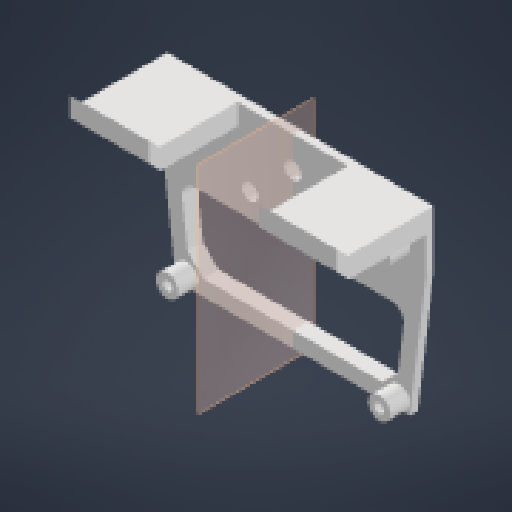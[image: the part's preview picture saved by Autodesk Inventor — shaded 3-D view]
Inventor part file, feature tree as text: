
AUTODESK INVENTOR PART (.ipt)
format: ipt  version: 2024 (Build 280153000, 153)  size: 214,528 bytes
history: native  units: in
note: dims shown in document units (in); Inventor stores cm internally (conversion verified against a paired STEP export)
features: other x4, extrude x3, sketch x3, reference x3, chamfer x2, fillet x1, mirror x1
ambient origin geometry x8: Origin, YZ Plane, XZ Plane, XY Plane, X Axis, Y Axis, Z Axis, Center Point
bodies: Solid1 (feature_tree)
feature tree (17):
  extrude  "Extrusion1"  Depth=0.1575in TaperAngle=0.0deg
  extrude  "Extrusion2"  Depth=1.5748in
  extrude  "Extrusion3"  Depth=0.125in
  chamfer  "Chamfer1"  Distance=1.5748in
  chamfer  "Chamfer2"  Distance=0.0787in
  fillet  "Fillet1"  Radius=0.1122in
  mirror  "Mirror1"
  sketch  "Sketch1"  dims[d0=0.1575in d1=0.1575in d2=0.0in]
  reference  "Reference1"
  reference  "Reference2"
  reference  "Reference3"
  sketch  "Sketch2"  dims[d3=2.3622in d4=1.5748in]
  sketch  "Sketch3"  dims[d5=0.1575in d6=2.3622in d7=1.5748in d8=0.0787in d9=0.1122in d10=0.1122in d11=0.0079in d12=0.1969in d13=0.0in d14=0.7874in d15=0.1575in d16=45.0deg d17=0.7874in d18=0.0in d19=0.125in d20=0.125in d21=45.0deg d22=0.0787in d23=0.125in d24=45.0deg d25=0.125in]
  other  "<userpath>\Desktop\SeniorDesign\Head_V3\Head_V3_Assembly.iam"
  other  "Head_V3_Assembly.iam"
  other  "Head_base_mount:1"
  other  "Head_Fin_Bottom:1"
